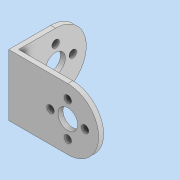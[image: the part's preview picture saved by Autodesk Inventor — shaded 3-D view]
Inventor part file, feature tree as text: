
AUTODESK INVENTOR PART (.ipt)
format: ipt  version: 2021.4 (Build 254397000, 397)  size: 139,264 bytes
history: native  units: in
note: dims shown in document units (in); Inventor stores cm internally (conversion verified against a paired STEP export)
features: extrude x3, sketch x2
ambient origin geometry x8: Origin, YZ Plane, XZ Plane, XY Plane, X Axis, Y Axis, Z Axis, Center Point
bodies: Solid1 (feature_tree)
feature tree (5):
  sketch  "Sketch1"  dims[d0=0.9449in d1=0.9843in]
  extrude  "Extrusion1"  Depth=0.9843in
  extrude  "Extrusion2"  Depth=0.0787in
  extrude  "Extrusion3"  Depth=0.0787in
  sketch  "Sketch2"  dims[d2=0.315in d3=0.5512in d4=0.1181in d5=1.5748in d7=360.0deg d9=0.0787in d10=0.0in d11=0.0787in d12=0.0394in d13=0.0in d14=0.5906in d15=0.9843in d16=0.315in d17=0.5512in d18=0.1181in d19=1.5748in d21=360.0deg d23=0.0787in d24=0.0in]
